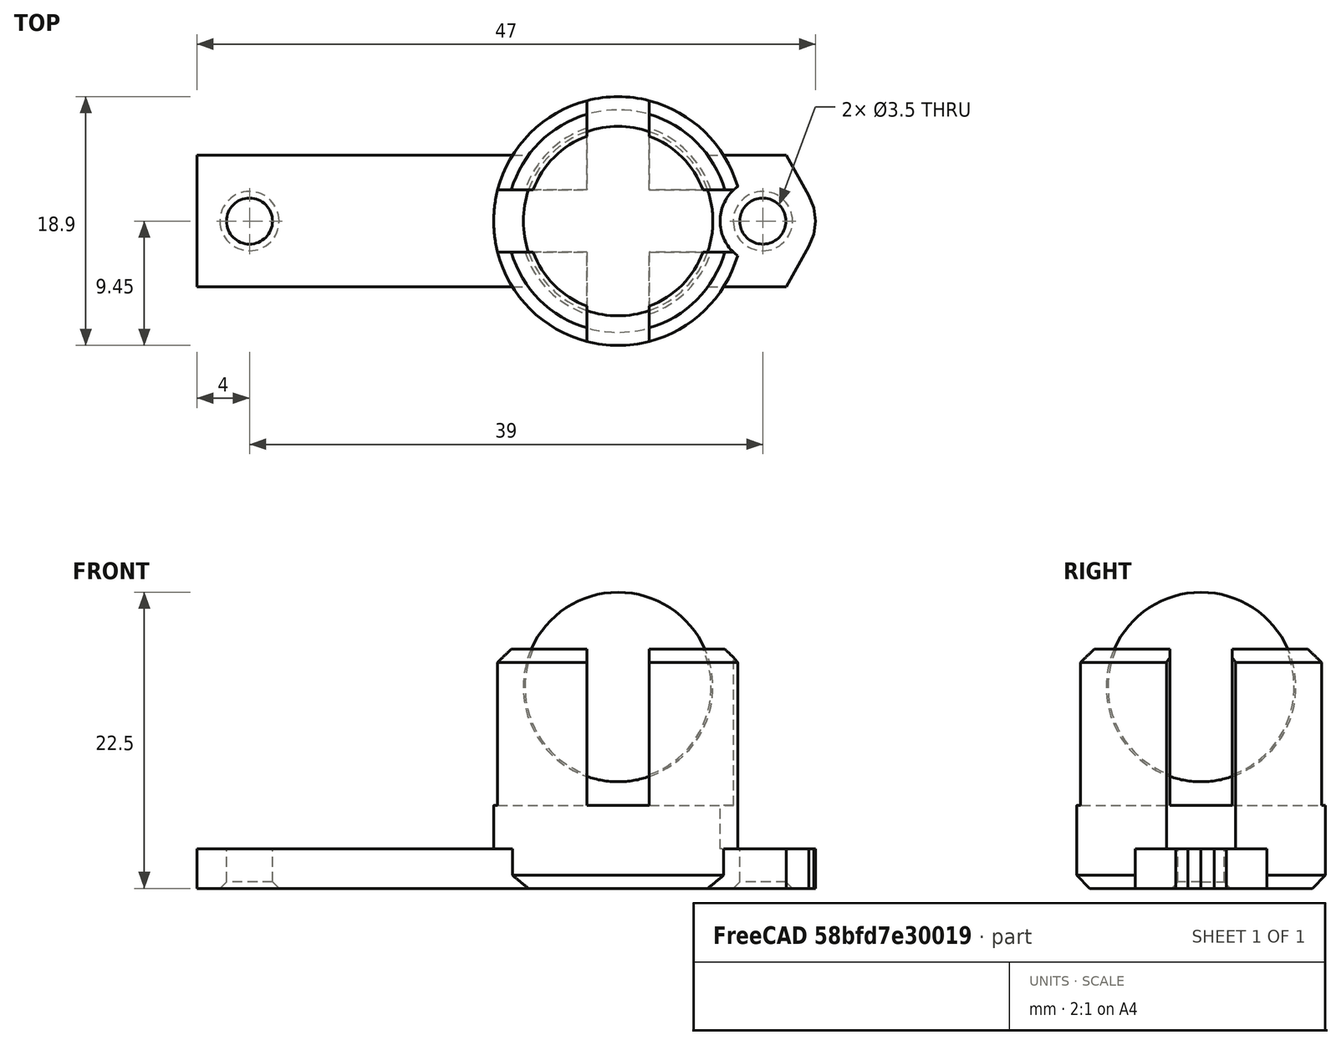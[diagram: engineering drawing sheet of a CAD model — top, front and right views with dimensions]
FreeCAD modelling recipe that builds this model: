
FCSTD DOCUMENT  (FreeCAD 0.14R3692 (Git))
Label: ballcaster
License: The MIT License
LicenseURL: http://opensource.org/licenses/MIT
objects: Part::Box×5, Part::Cylinder×5, Part::Fuse×5, Part::FeaturePython×3, Part::Cut×3, Part::Cone×2, Part::MultiFuse×2, Part::Sphere×2, Part::Chamfer×1, Part::Feature×1, App::DocumentObjectGroup×1
note: 29 computed .brp shape members not serialized (recipe doc carries the construction recipe); baked Part::Feature solids carry a one-line shape summary decoded from their .brp

FEATURE [Part::Box] cube
  Height = 3
  Length = 42
  Placement = pos=(-4,-10,-1.5) rot=(0,0,1;0rad)
  Width = 20
FEATURE [Part::Cylinder] cylinder
  Angle = 360
  Height = 3
  Placement = pos=(39,0,-1.5) rot=(0,0,1;0rad)
  Radius = 4
FEATURE [Part::FeaturePython] hull  # WARN: FeaturePython — macro-defined, semantics opaque (R4)
  Arguments = []
  Children = -> [cube,cylinder]
  Operation = hull
FEATURE [Part::Box] cube001
  Height = 4
  Length = 86
  Placement = pos=(-43,5,-2) rot=(0,0,1;0rad)
  Width = 10
FEATURE [Part::Box] cube002
  Height = 4
  Length = 86
  Placement = pos=(-43,-15,-2) rot=(0,0,1;0rad)
  Width = 10
FEATURE [Part::Fuse] Group
  Base = -> cube001
  Tool = -> cube002
FEATURE [Part::Cut] difference
  Base = -> hull
  Tool = -> Group
FEATURE [Part::Cylinder] cylinder001
  Angle = 360
  Height = 16.18
  Placement = pos=(0,0,1) rot=(0,0,1;0rad)
  Radius = 9.45
FEATURE [Part::Cone] cylinder002
  Angle = 360
  Height = 1
  Radius1 = 8.45
  Radius2 = 9.45
FEATURE [Part::Cone] cylinder003
  Angle = 360
  Height = 1
  Placement = pos=(0,0,17.18) rot=(0,0,1;0rad)
  Radius1 = 9.45
  Radius2 = 8.45
FEATURE [Part::MultiFuse] union
  Shapes = -> [cylinder001,cylinder002,cylinder003]
FEATURE [Part::Box] cube003
  Height = 18
  Length = 23.9
  Placement = pos=(-11.95,-2.3625,-9) rot=(0,0,1;0rad)
  Width = 4.725
FEATURE [Part::Box] cube004
  Height = 18
  Length = 23.9
  Placement = pos=(2.3625,-11.95,-9) rot=(0,0,1;1.5708rad)
  Width = 4.725
FEATURE [Part::Fuse] Group001
  Base = -> cube003
  Placement = pos=(0,0,15.3) rot=(0,0,1;0rad)
  Tool = -> cube004
FEATURE [Part::Sphere] sphere
  Angle1 = -90
  Angle2 = 90
  Angle3 = 360
  Radius = 7.2
FEATURE [Part::Sphere] sphere001
  Angle1 = -90
  Angle2 = 90
  Angle3 = 360
  Radius = 7.45
FEATURE [Part::Fuse] Matrix_Union
  Base = -> sphere
  Placement = pos=(0,0,15.3) rot=(0,0,1;0rad)
  Tool = -> sphere001
FEATURE [Part::Fuse] union001
  Base = -> Group001
  Tool = -> Matrix_Union
FEATURE [Part::Cut] difference001
  Base = -> union
  Placement = pos=(28,0,-1.5) rot=(0,0,1;0rad)
  Tool = -> union001
FEATURE [Part::Fuse] union002
  Base = -> difference
  Tool = -> difference001
FEATURE [Part::Cylinder] cylinder004
  Angle = 360
  Height = 4
  Placement = pos=(0,0,-2) rot=(0,0,1;0rad)
  Radius = 1.75
FEATURE [Part::Cylinder] cylinder005
  Angle = 360
  Height = 4
  Placement = pos=(39,0,-2) rot=(0,0,1;0rad)
  Radius = 1.75
FEATURE [Part::Cylinder] cylinder006
  Angle = 360
  Height = 20
  Placement = pos=(39,0,1.5) rot=(0,0,1;0rad)
  Radius = 3.25
FEATURE [Part::MultiFuse] Group002
  Shapes = -> [cylinder004,cylinder005,cylinder006]
FEATURE [Part::Cut] difference002
  Base = -> union002
  Tool = -> Group002
FEATURE [Part::FeaturePython] Clone  label="ballcaster"  # Draft clone (typed FeaturePython)
  Objects = -> [difference002]
  Scale = (1,1,1)
FEATURE [Part::Chamfer] Chamfer  label="printing-chamfer"
  Base = -> Clone
  Edges = 4 edges r=0.5: [Edge11,Edge12,Edge13,Edge14]
FEATURE [Part::FeaturePython] Clone001  label="ballcaster (printing)"  # Draft clone (typed FeaturePython)
  Objects = -> [Chamfer]
  Scale = (1,1,1)
FEATURE [Part::Feature] Part__Feature  label="ball"
  Placement = pos=(28,0,13.8) rot=(0,0,1;0rad)
  shape: bbox 14.4 x 14.4 x 14.4 mm, 1 faces (baked)
FEATURE [App::DocumentObjectGroup] Group003  label="components"
  Group = -> [Part__Feature]
